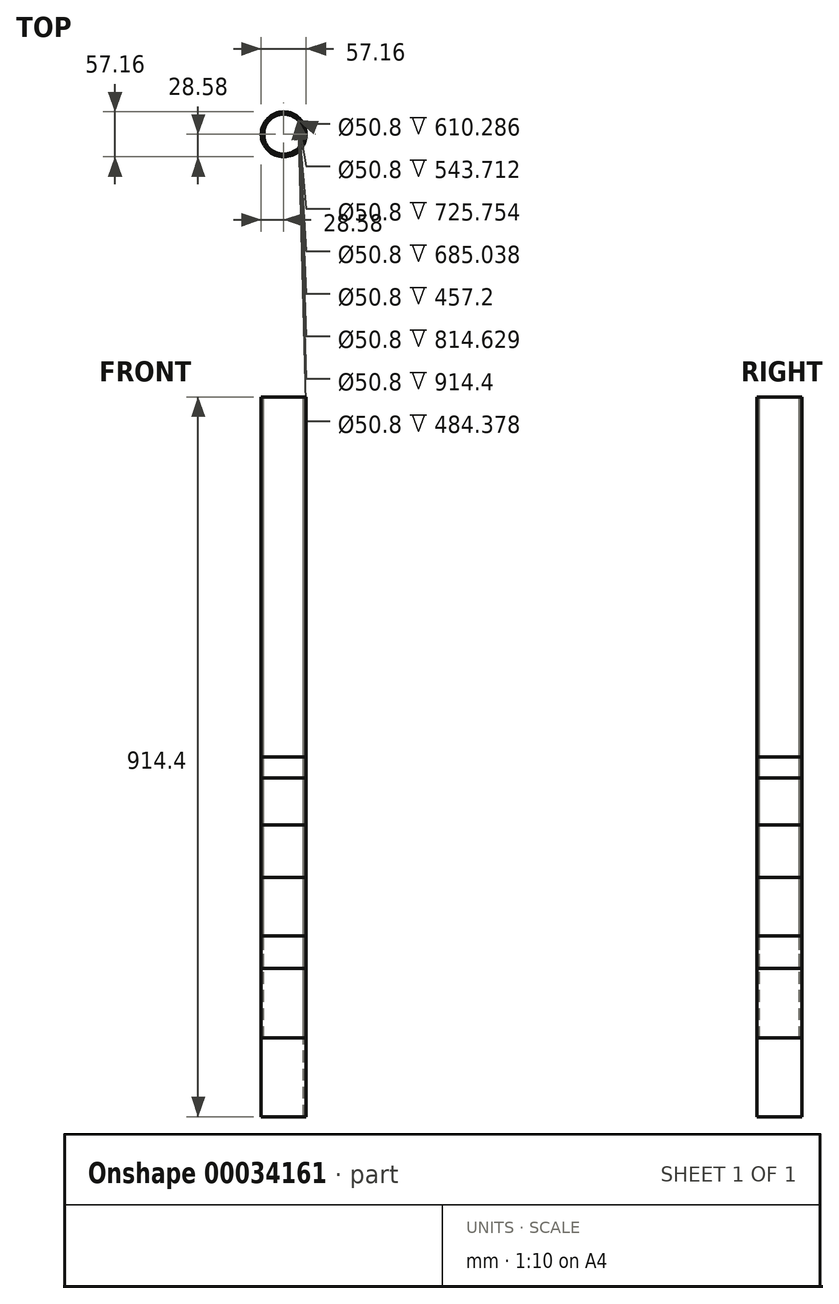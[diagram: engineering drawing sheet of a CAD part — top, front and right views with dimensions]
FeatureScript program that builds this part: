
annotation { "Feature Type Name" : "Feature", "Feature Type Description" : "" }
export const myFeature = defineFeature(function(context is Context, id is Id, definition is map)
    precondition{}
    {
        {
            var Q0;
            Q0=qCreatedBy(makeId("Top.planeOp"),FACE);
            var sketch = newSketch(context, id + "F0", { "sketchPlane" : qUnion([Q0])});
            skCircle(sketch, "E0", {"center": v(0, 0) * mm, "radius": 25.4 * mm});
            skCircle(sketch, "E1", {"center": v(0, 0) * mm, "radius": 28.58 * mm});
            skSolve(sketch);
        }
        {
            var Q0;
            Q0=makeQuery(id+"F0.imprint","IMPRINT",FACE,{"disambiguationData":[TD([[makeQuery(id+"F0.imprint","IMPRINT",EDGE,{"derivedFrom":sQuery(id+"F0.wireOp",EDGE,"E0")}),-1.0]])]});
            extrude(context, id + "F1", {"entities" : qUnion([Q0]), "oppositeDirection" : true, "depth" : 914.4 * mm});
        }
        {
            var Q0;
            Q0=makeQuery(id+"F1.opExtrude","CAP_FACE",FACE,{"disambiguationData":[OSD([sQuery(id+"F0.wireOp",EDGE,"E0"),sQuery(id+"F0.wireOp",EDGE,"E1")])],"isStart":true});
            extrude(context, id + "F2", {"entities" : qUnion([Q0]), "oppositeDirection" : true, "depth" : 457.2 * mm});
        }
        {
            var Q0;
            Q0=qSketchRegion(id+"F0",true);
            extrude(context, id + "F3", {"entities" : qUnion([Q0]), "oppositeDirection" : true, "depth" : 814.63 * mm});
        }
        {
            var Q0;
            Q0=qSketchRegion(id+"F0",true);
            extrude(context, id + "F4", {"entities" : qUnion([Q0]), "oppositeDirection" : true, "depth" : 725.75 * mm});
        }
        {
            var Q0;
            Q0=qSketchRegion(id+"F0",true);
            extrude(context, id + "F5", {"entities" : qUnion([Q0]), "oppositeDirection" : true, "depth" : 685.04 * mm});
        }
        {
            var Q0;
            Q0=qSketchRegion(id+"F0",true);
            extrude(context, id + "F6", {"entities" : qUnion([Q0]), "oppositeDirection" : true, "depth" : 610.3 * mm});
        }
        {
            var Q0;
            Q0=qSketchRegion(id+"F0",true);
            extrude(context, id + "F7", {"entities" : qUnion([Q0]), "oppositeDirection" : true, "depth" : 543.7 * mm});
        }
        {
            var Q0;
            Q0=qSketchRegion(id+"F0",true);
            extrude(context, id + "F8", {"entities" : qUnion([Q0]), "oppositeDirection" : true, "depth" : 484.38 * mm});
        }
    });
